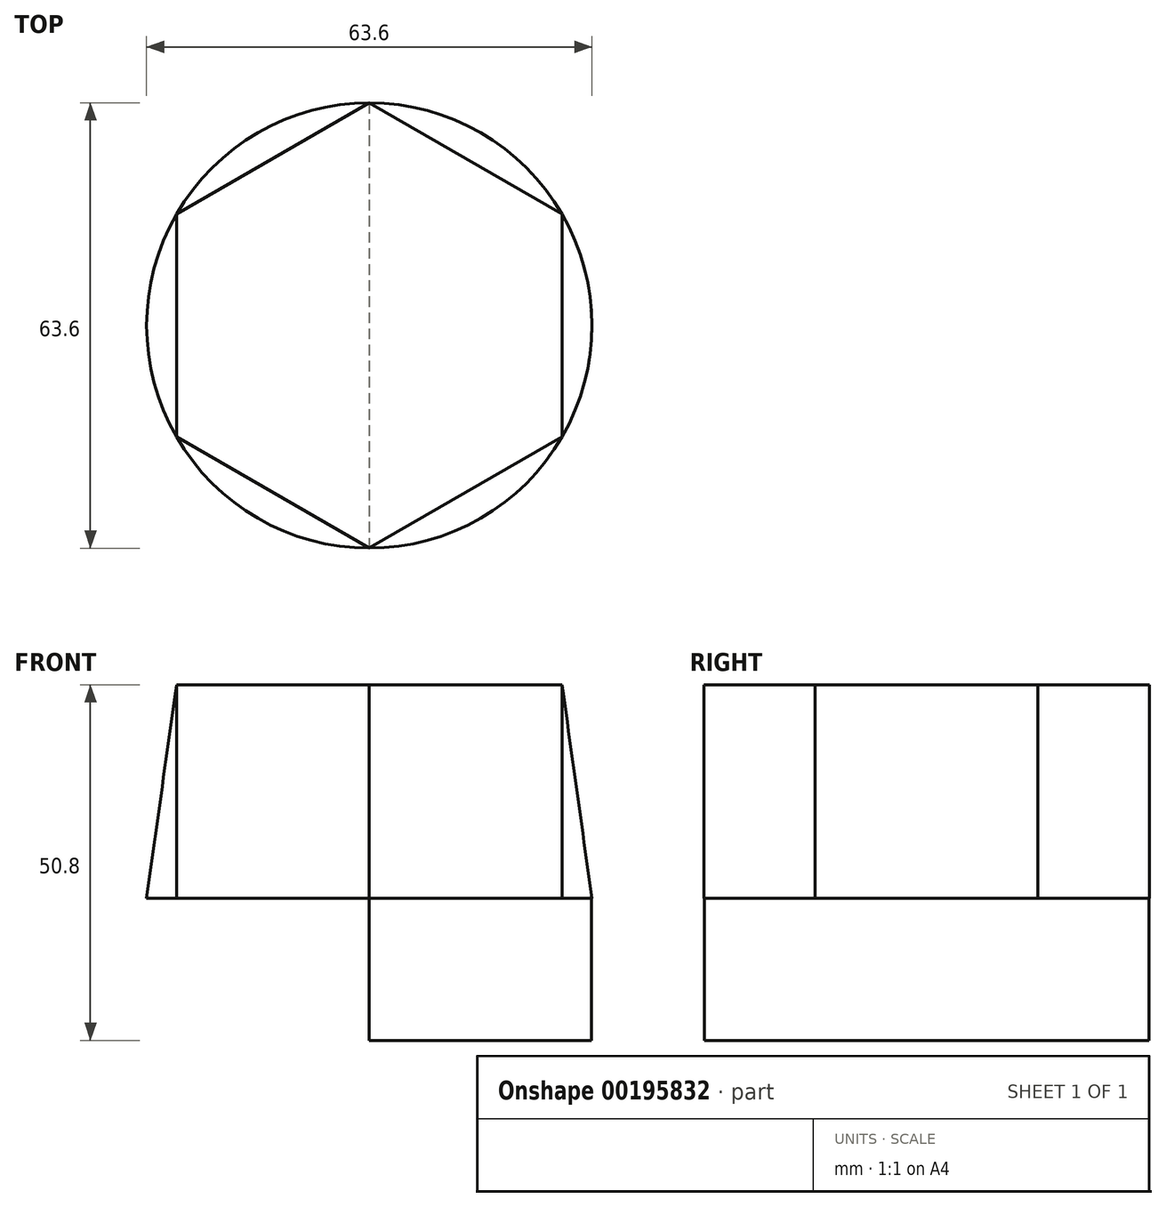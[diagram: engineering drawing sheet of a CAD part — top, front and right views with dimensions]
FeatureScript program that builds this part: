
annotation { "Feature Type Name" : "Feature", "Feature Type Description" : "" }
export const myFeature = defineFeature(function(context is Context, id is Id, definition is map)
    precondition{}
    {
        {
            var Q0;
            Q0=qCreatedBy(makeId("Top.planeOp"),FACE);
            var sketch = newSketch(context, id + "F0", { "sketchPlane" : qUnion([Q0])});
            skLineSegment(sketch, "E0", {"start": v(0, 31.75) * mm, "end": v(0, -31.75) * mm});
            skArc(sketch, "E1", {"start": v(0, -31.75) * mm, "mid": v(31.75, 0) * mm, "end": v(0, 31.75) * mm});
            skSolve(sketch);
        }
        {
            var Q0;
            Q0=makeQuery(id+"F0.imprint","IMPRINT",FACE,{"disambiguationData":[TD([[makeQuery(id+"F0.imprint","IMPRINT",EDGE,{"derivedFrom":sQuery(id+"F0.wireOp",EDGE,"iQHm4Ffv-Fe6U-kdTP-Zalh-QQHW2kFpvTAs")}),1.0]])]});
            var Q1;
            Q1=makeQuery(id+"F0.imprint","IMPRINT",FACE,{"disambiguationData":[TD([[makeQuery(id+"F0.imprint","IMPRINT",EDGE,{"derivedFrom":sQuery(id+"F0.wireOp",EDGE,"E0")}),1.0]])]});
            extrude(context, id + "F1", {"entities" : qUnion([Q0, Q1]), "depth" : 20.32 * mm});
        }
        {
            var Q0;
            Q0=makeQuery(id+"F1.opExtrude","CAP_FACE",FACE,{"disambiguationData":[OSD([sQuery(id+"F0.wireOp",EDGE,"E0"),sQuery(id+"F0.wireOp",EDGE,"E1")])],"isStart":false});
            cPlane(context, id + "F2", {"entities" : qUnion([Q0]), "cplaneType" : CPlaneType.OFFSET, "offset" : 0 * mm, "width" : 152.4 * mm, "height" : 152.4 * mm});
        }
        {
            var Q0;
            Q0=qCreatedBy(id+"F2.planeOp",FACE);
            cPlane(context, id + "F3", {"entities" : qUnion([Q0]), "cplaneType" : CPlaneType.OFFSET, "offset" : 30.48 * mm, "width" : 152.4 * mm, "height" : 152.4 * mm});
        }
        {
            var Q0;
            Q0=qCreatedBy(id+"F2.planeOp",FACE);
            var sketch = newSketch(context, id + "F4", { "sketchPlane" : qUnion([Q0])});
            skCircle(sketch, "E2", {"center": v(0, 0) * mm, "radius": 31.8 * mm});
            skSolve(sketch);
        }
        {
            var Q0;
            Q0=qCreatedBy(id+"F3.planeOp",FACE);
            var sketch = newSketch(context, id + "F5", { "sketchPlane" : qUnion([Q0])});
            skCircle(sketch, "E3.cCircle", {"center": v(0, 0) * mm, "radius": 31.8 * mm, "construction": true});
            skLineSegment(sketch, "E3.0", {"start": v(0, 31.8) * mm, "end": v(27.54, 15.9) * mm});
            skLineSegment(sketch, "E3.1", {"start": v(27.54, 15.9) * mm, "end": v(27.54, -15.9) * mm});
            skLineSegment(sketch, "E3.2", {"start": v(27.54, -15.9) * mm, "end": v(0, -31.8) * mm});
            skLineSegment(sketch, "E3.3", {"start": v(0, -31.8) * mm, "end": v(-27.54, -15.9) * mm});
            skLineSegment(sketch, "E3.4", {"start": v(-27.54, -15.9) * mm, "end": v(-27.54, 15.9) * mm});
            skLineSegment(sketch, "E3.5", {"start": v(-27.54, 15.9) * mm, "end": v(0, 31.8) * mm});
            skSolve(sketch);
        }
        {
            var Q1;
            Q1=makeQuery(id+"F4.imprint","IMPRINT",FACE,{"disambiguationData":[TD([[makeQuery(id+"F4.imprint","IMPRINT",EDGE,{"derivedFrom":sQuery(id+"F4.wireOp",EDGE,"E2")}),1.0]])]});
            var Q2;
            Q2=makeQuery(id+"F5.imprint","IMPRINT",FACE,{"disambiguationData":[TD([[makeQuery(id+"F5.imprint","IMPRINT",EDGE,{"derivedFrom":sQuery(id+"F5.wireOp",EDGE,"E3.0")}),-1.0]])]});
            loft(context, id + "F6", {"operationType" : NewBodyOperationType.ADD, "sheetProfilesArray" : [{ "sheetProfileEntities" : qUnion([Q1]) }, { "sheetProfileEntities" : qUnion([Q2]) }]});
        }
        {
            var Q0;
            Q0=qCreatedBy(id+"F3.planeOp",FACE);
            var sketch = newSketch(context, id + "F7", { "sketchPlane" : qUnion([Q0])});
            skPoint(sketch, "E4.0", {"position": v(27.54, -15.9) * mm});
            skPoint(sketch, "E5.0", {"position": v(0, -31.8) * mm});
            skPoint(sketch, "E6.0", {"position": v(27.54, 15.9) * mm});
            skPoint(sketch, "E7.0", {"position": v(0, 31.8) * mm});
            skPoint(sketch, "E8.0", {"position": v(-27.54, 15.9) * mm});
            skPoint(sketch, "E9.0", {"position": v(-27.54, -15.9) * mm});
            skLineSegment(sketch, "E10.0", {"start": v(-27.54, 15.9) * mm, "end": v(-27.54, -15.9) * mm, "construction": true});
            skLineSegment(sketch, "E11.0", {"start": v(-27.54, -15.9) * mm, "end": v(0, -31.8) * mm, "construction": true});
            skLineSegment(sketch, "E12.0.0", {"start": v(27.54, 15.9) * mm, "end": v(0, 31.8) * mm, "construction": true});
            skLineSegment(sketch, "E12.0.1", {"start": v(0, 31.8) * mm, "end": v(-27.54, 15.9) * mm, "construction": true});
            skLineSegment(sketch, "E12.0.4", {"start": v(0, -31.8) * mm, "end": v(27.54, -15.9) * mm, "construction": true});
            skLineSegment(sketch, "E12.0.5", {"start": v(27.54, -15.9) * mm, "end": v(27.54, 15.9) * mm, "construction": true});
            skLineSegment(sketch, "E13", {"start": v(27.54, -15.9) * mm, "end": v(-27.54, 15.9) * mm, "construction": true});
            skLineSegment(sketch, "E14", {"start": v(27.54, 15.9) * mm, "end": v(-27.54, -15.9) * mm, "construction": true});
            skLineSegment(sketch, "E15", {"start": v(0, -31.8) * mm, "end": v(0, 31.8) * mm, "construction": true});
            skPoint(sketch, "E16", {"position": v(0, 0) * mm});
            skCircle(sketch, "E17", {"center": v(0, 0) * mm, "radius": 31.8 * mm, "construction": true});
            skCircle(sketch, "E18", {"center": v(0, 0) * mm, "radius": 27.54 * mm, "construction": true});
            skCircle(sketch, "E19", {"center": v(0, -23.73) * mm, "radius": 3.81 * mm});
            skCircle(sketch, "E20", {"center": v(-20.55, -11.86) * mm, "radius": 3.81 * mm});
            skCircle(sketch, "E21", {"center": v(-20.55, 11.86) * mm, "radius": 3.81 * mm});
            skCircle(sketch, "E22", {"center": v(0, 23.73) * mm, "radius": 3.81 * mm});
            skCircle(sketch, "E23", {"center": v(20.55, 11.86) * mm, "radius": 3.81 * mm});
            skCircle(sketch, "E24", {"center": v(20.55, -11.86) * mm, "radius": 3.81 * mm});
            skPoint(sketch, "E25", {"position": v(0, -27.54) * mm});
            skPoint(sketch, "E26", {"position": v(-23.85, -13.77) * mm});
            skPoint(sketch, "E27", {"position": v(-23.85, 13.77) * mm});
            skPoint(sketch, "E28", {"position": v(0, 27.54) * mm});
            skPoint(sketch, "E29", {"position": v(23.85, 13.77) * mm});
            skPoint(sketch, "E30", {"position": v(23.85, -13.77) * mm});
            skSolve(sketch);
        }
        {
            var Q0;
            Q0=qCreatedBy(id+"F3.planeOp",FACE);
            cPlane(context, id + "F8", {"entities" : qUnion([Q0]), "cplaneType" : CPlaneType.OFFSET, "offset" : 12.7 * mm, "width" : 152.4 * mm, "height" : 152.4 * mm});
        }
        {
            var Q0;
            Q0=qCreatedBy(id+"F8.planeOp",FACE);
            cPlane(context, id + "F9", {"entities" : qUnion([Q0]), "cplaneType" : CPlaneType.OFFSET, "offset" : 6.35 * mm, "width" : 152.4 * mm, "height" : 152.4 * mm});
        }
        {
            var Q0;
            Q0=qCreatedBy(id+"F9.planeOp",FACE);
            var sketch = newSketch(context, id + "F10", { "sketchPlane" : qUnion([Q0])});
            skCircle(sketch, "E31", {"center": v(0, 0) * mm, "radius": 31.8 * mm});
            skSolve(sketch);
        }
        {
            var Q0;
            Q0=qCreatedBy(id+"F9.planeOp",FACE);
            cPlane(context, id + "F11", {"entities" : qUnion([Q0]), "cplaneType" : CPlaneType.OFFSET, "offset" : 30.48 * mm, "width" : 152.4 * mm, "height" : 152.4 * mm});
        }
    });
